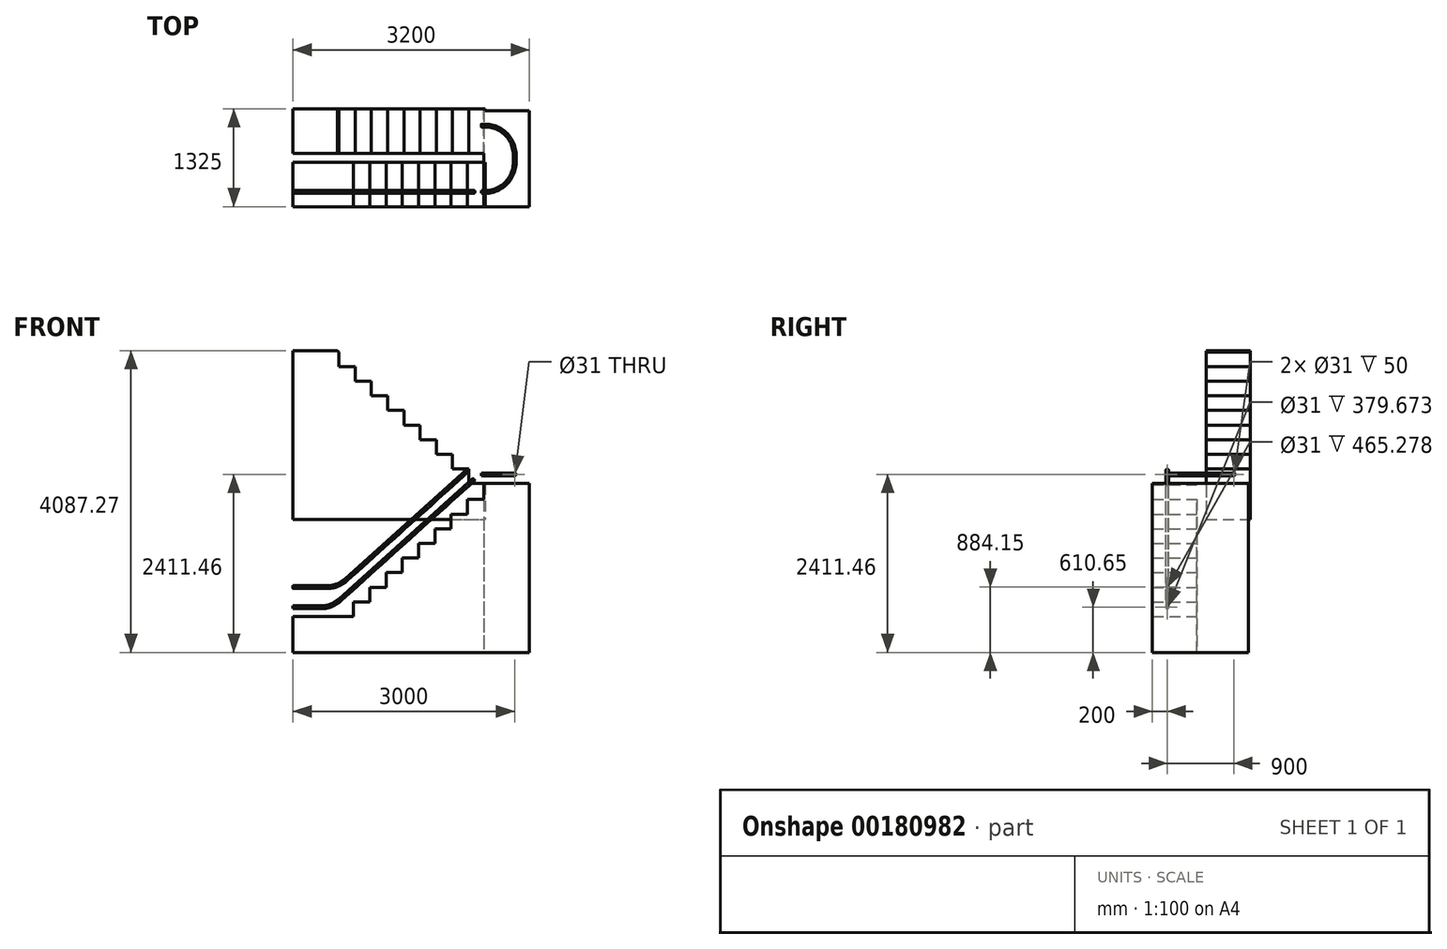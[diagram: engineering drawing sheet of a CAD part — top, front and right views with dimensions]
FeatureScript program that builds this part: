
annotation { "Feature Type Name" : "Feature", "Feature Type Description" : "" }
export const myFeature = defineFeature(function(context is Context, id is Id, definition is map)
    precondition{}
    {
        {
            var Q0;
            Q0=qCreatedBy(makeId("Front.planeOp"),FACE);
            var sketch = newSketch(context, id + "F0", { "sketchPlane" : qUnion([Q0])});
            skLineSegment(sketch, "E0", {"start": v(0, 0) * mm, "end": v(600, 0) * mm});
            skLineSegment(sketch, "E1", {"start": v(600, 0) * mm, "end": v(2600, 1800.8) * mm, "construction": true});
            skLineSegment(sketch, "E2", {"start": v(2600, 1800.8) * mm, "end": v(3200, 1800.8) * mm});
            skLineSegment(sketch, "E3", {"start": v(600, 0) * mm, "end": v(3446.75, 0) * mm, "construction": true});
            skLineSegment(sketch, "E4", {"start": v(716.2, 494.82) * mm, "end": v(803.08, 573.04) * mm});
            skPoint(sketch, "E5", {"position": v(759.64, 533.93) * mm});
            skPoint(sketch, "E6", {"position": v(655.57, 303.01) * mm});
            skCircle(sketch, "E7", {"center": v(655.57, 303.01) * mm, "radius": 25 * mm});
            skLineSegment(sketch, "E8", {"start": v(483.42, 114.37) * mm, "end": v(1236.08, 792.07) * mm});
            skLineSegment(sketch, "E9", {"start": v(627.76, 193.2) * mm, "end": v(1325.27, 821.24) * mm});
            skLineSegment(sketch, "E10", {"start": v(1036.91, 758.02) * mm, "end": v(1656.58, 1315.97) * mm});
            skLineSegment(sketch, "E11", {"start": v(940.91, 722.72) * mm, "end": v(2243.48, 1895.55) * mm});
            skLineSegment(sketch, "E12", {"start": v(415.28, 398.5) * mm, "end": v(465.28, 398.5) * mm});
            skArc(sketch, "E13", {"start": v(465.28, 398.5) * mm, "mid": v(599.67, 423.4) * mm, "end": v(716.2, 494.82) * mm});
            skLineSegment(sketch, "E14", {"start": v(465.28, 398.5) * mm, "end": v(465.28, 773.5) * mm, "construction": true});
            skLineSegment(sketch, "E15", {"start": v(465.28, 773.5) * mm, "end": v(716.2, 494.82) * mm, "construction": true});
            skLineSegment(sketch, "E16", {"start": v(0, 0) * mm, "end": v(0, 732.21) * mm, "construction": true});
            skLineSegment(sketch, "E17", {"start": v(415.28, 398.5) * mm, "end": v(0, 398.5) * mm});
            skLineSegment(sketch, "E18", {"start": v(630.6, 221.32) * mm, "end": v(1225.2, 756.7) * mm});
            skArc(sketch, "E19", {"start": v(379.67, 125) * mm, "mid": v(514.06, 149.9) * mm, "end": v(630.6, 221.32) * mm});
            skLineSegment(sketch, "E20", {"start": v(379.67, 125) * mm, "end": v(379.67, 500) * mm, "construction": true});
            skLineSegment(sketch, "E21", {"start": v(379.67, 500) * mm, "end": v(630.6, 221.32) * mm, "construction": true});
            skLineSegment(sketch, "E22", {"start": v(379.67, 125) * mm, "end": v(329.67, 125) * mm});
            skLineSegment(sketch, "E23", {"start": v(329.67, 125) * mm, "end": v(0, 125) * mm});
            skLineSegment(sketch, "E24", {"start": v(759.64, 533.93) * mm, "end": v(827.87, 458.15) * mm, "construction": true});
            skLineSegment(sketch, "E25", {"start": v(827.87, 458.15) * mm, "end": v(655.57, 303.01) * mm, "construction": true});
            skLineSegment(sketch, "E26", {"start": v(759.64, 533.93) * mm, "end": v(655.57, 303.01) * mm, "construction": true});
            skLineSegment(sketch, "E27", {"start": v(600, 0) * mm, "end": v(820, 0) * mm});
            skLineSegment(sketch, "E28", {"start": v(820, 0) * mm, "end": v(820, 198.09) * mm});
            skLineSegment(sketch, "E29", {"start": v(820, 198.09) * mm, "end": v(1040, 198.09) * mm});
            skLineSegment(sketch, "E30", {"start": v(1040, 198.09) * mm, "end": v(1040, 396.18) * mm});
            skLineSegment(sketch, "E31", {"start": v(1040, 396.18) * mm, "end": v(1260, 396.18) * mm});
            skLineSegment(sketch, "E32", {"start": v(1260, 396.18) * mm, "end": v(1260, 594.27) * mm});
            skLineSegment(sketch, "E33", {"start": v(3200, 1800.8) * mm, "end": v(3200, -485.65) * mm});
            skLineSegment(sketch, "E34", {"start": v(3200, -485.65) * mm, "end": v(0, -485.65) * mm});
            skLineSegment(sketch, "E35", {"start": v(0, -485.65) * mm, "end": v(0, 0) * mm});
            skPoint(sketch, "E36.start.orphan", {"position": v(1600, 900.4) * mm});
            skLineSegment(sketch, "E37", {"start": v(1260, 594.27) * mm, "end": v(1480, 594.27) * mm});
            skLineSegment(sketch, "E38", {"start": v(1480, 594.27) * mm, "end": v(1480, 792.36) * mm});
            skLineSegment(sketch, "E39", {"start": v(1480, 792.36) * mm, "end": v(1700, 792.36) * mm});
            skLineSegment(sketch, "E40", {"start": v(1700, 792.36) * mm, "end": v(1700, 990.44) * mm});
            skLineSegment(sketch, "E41", {"start": v(1700, 990.44) * mm, "end": v(1920, 990.44) * mm});
            skLineSegment(sketch, "E42", {"start": v(1920, 990.44) * mm, "end": v(1920, 1188.53) * mm});
            skLineSegment(sketch, "E43", {"start": v(1920, 1188.53) * mm, "end": v(2140, 1188.53) * mm});
            skLineSegment(sketch, "E44", {"start": v(2140, 1188.53) * mm, "end": v(2140, 1386.62) * mm});
            skLineSegment(sketch, "E45", {"start": v(2140, 1386.62) * mm, "end": v(2360, 1386.62) * mm});
            skLineSegment(sketch, "E46", {"start": v(2360, 1386.62) * mm, "end": v(2360, 1584.71) * mm});
            skLineSegment(sketch, "E47", {"start": v(2360, 1584.71) * mm, "end": v(2580, 1584.71) * mm});
            skLineSegment(sketch, "E48", {"start": v(2580, 1584.71) * mm, "end": v(2580, 1782.8) * mm});
            skLineSegment(sketch, "E49", {"start": v(2580, 1782.8) * mm, "end": v(2600, 1800.8) * mm});
            skLineSegment(sketch, "E50", {"start": v(803.08, 573.04) * mm, "end": v(2366.72, 1980.95) * mm});
            skLineSegment(sketch, "E51", {"start": v(1225.2, 756.7) * mm, "end": v(2449.59, 1859.15) * mm});
            skSolve(sketch);
        }
        {
            var Q0;
            Q0=qCreatedBy(makeId("Right.planeOp"),FACE);
            var sketch = newSketch(context, id + "F1", { "sketchPlane" : qUnion([Q0])});
            skLineSegment(sketch, "E52", {"start": v(0, 0) * mm, "end": v(0, 398.5) * mm, "construction": true});
            skPoint(sketch, "E53", {"position": v(0, 125) * mm});
            skCircle(sketch, "E54", {"center": v(0, 398.5) * mm, "radius": 19 * mm});
            skCircle(sketch, "E55", {"center": v(0, 125) * mm, "radius": 19 * mm});
            skCircle(sketch, "E56.0", {"center": v(0, 398.5) * mm, "radius": 15.5 * mm});
            skCircle(sketch, "E57.0", {"center": v(0, 125) * mm, "radius": 15.5 * mm});
            skSolve(sketch);
        }
        {
            var Q0;
            Q0=makeQuery(id+"F1.imprint","IMPRINT",FACE,{"disambiguationData":[TD([[makeQuery(id+"F1.imprint","IMPRINT",EDGE,{"derivedFrom":sQuery(id+"F1.wireOp",EDGE,"E54")}),1.0]])]});
            var Q1;
            Q1=sQuery(id+"F0.wireOp",EDGE,"E17");
            var Q2;
            Q2=sQuery(id+"F0.wireOp",EDGE,"E12");
            var Q3;
            Q3=sQuery(id+"F0.wireOp",EDGE,"E13");
            var Q4;
            Q4=sQuery(id+"F0.wireOp",EDGE,"E4");
            var Q5;
            Q5=sQuery(id+"F0.wireOp",EDGE,"E50");
            sweep(context, id + "F2", {"profiles" : qUnion([Q0]), "path" : qUnion([Q1, Q2, Q3, Q4, Q5])});
        }
        {
            var Q0;
            Q0=makeQuery(id+"F1.imprint","IMPRINT",FACE,{"disambiguationData":[TD([[makeQuery(id+"F1.imprint","IMPRINT",EDGE,{"derivedFrom":sQuery(id+"F1.wireOp",EDGE,"E55")}),1.0]])]});
            var Q1;
            Q1=sQuery(id+"F0.wireOp",EDGE,"E23");
            var Q2;
            Q2=sQuery(id+"F0.wireOp",EDGE,"E22");
            var Q3;
            Q3=sQuery(id+"F0.wireOp",EDGE,"E19");
            var Q4;
            Q4=sQuery(id+"F0.wireOp",EDGE,"E18");
            var Q5;
            Q5=sQuery(id+"F0.wireOp",EDGE,"E51");
            sweep(context, id + "F3", {"profiles" : qUnion([Q0]), "path" : qUnion([Q1, Q2, Q3, Q4, Q5])});
        }
        {
            var Q0;
            Q0=makeQuery(id+"F0.imprint","IMPRINT",FACE,{"disambiguationData":[TD([[makeQuery(id+"F0.imprint","IMPRINT",EDGE,{"derivedFrom":sQuery(id+"F0.wireOp",EDGE,"E0")}),-1.0]])]});
            extrude(context, id + "F4", {"entities" : qUnion([Q0]), "depth" : 200 * mm, "hasSecondDirection" : true, "secondDirectionOppositeDirection" : true, "secondDirectionDepth" : 400 * mm});
        }
        {
            var Q0;
            Q0=makeQuery(id+"F4.opExtrude","CAP_FACE",FACE,{"disambiguationData":[OSD([sQuery(id+"F0.wireOp",EDGE,"E0"),sQuery(id+"F0.wireOp",EDGE,"E2"),sQuery(id+"F0.wireOp",EDGE,"E27"),sQuery(id+"F0.wireOp",EDGE,"E28"),sQuery(id+"F0.wireOp",EDGE,"E29"),sQuery(id+"F0.wireOp",EDGE,"E30"),sQuery(id+"F0.wireOp",EDGE,"E31"),sQuery(id+"F0.wireOp",EDGE,"E32"),sQuery(id+"F0.wireOp",EDGE,"E33"),sQuery(id+"F0.wireOp",EDGE,"E34"),sQuery(id+"F0.wireOp",EDGE,"E35"),sQuery(id+"F0.wireOp",EDGE,"E37"),sQuery(id+"F0.wireOp",EDGE,"E38"),sQuery(id+"F0.wireOp",EDGE,"E39"),sQuery(id+"F0.wireOp",EDGE,"E40"),sQuery(id+"F0.wireOp",EDGE,"E41"),sQuery(id+"F0.wireOp",EDGE,"E42"),sQuery(id+"F0.wireOp",EDGE,"E43"),sQuery(id+"F0.wireOp",EDGE,"E44"),sQuery(id+"F0.wireOp",EDGE,"E45"),sQuery(id+"F0.wireOp",EDGE,"E46"),sQuery(id+"F0.wireOp",EDGE,"E47"),sQuery(id+"F0.wireOp",EDGE,"E48"),sQuery(id+"F0.wireOp",EDGE,"E49")])],"isStart":true});
            var sketch = newSketch(context, id + "F5", { "sketchPlane" : qUnion([Q0])});
            skLineSegment(sketch, "E58.bottom", {"start": v(-3200, 1800.8) * mm, "end": v(-2580, 1800.8) * mm});
            skLineSegment(sketch, "E58.top", {"start": v(-3200, -485.65) * mm, "end": v(-2580, -485.65) * mm});
            skLineSegment(sketch, "E58.left", {"start": v(-3200, 1800.8) * mm, "end": v(-3200, -485.65) * mm});
            skLineSegment(sketch, "E58.right", {"start": v(-2580, 1800.8) * mm, "end": v(-2580, -485.65) * mm});
            skSolve(sketch);
        }
        {
            var Q0;
            Q0 = qSketchRegion(id + "F5", true);
            extrude(context, id + "F6", {"entities" : qUnion([Q0]), "operationType" : NewBodyOperationType.ADD, "depth" : 700 * mm});
        }
        {
            var Q0;
            Q0=makeQuery(id+"F6.opExtrude","CAP_FACE",FACE,{"disambiguationData":[OSD([sQuery(id+"F5.wireOp",EDGE,"E58.bottom"),sQuery(id+"F5.wireOp",EDGE,"E58.top"),sQuery(id+"F5.wireOp",EDGE,"E58.left"),sQuery(id+"F5.wireOp",EDGE,"E58.right")])],"isStart":false});
            cPlane(context, id + "F7", {"entities" : qUnion([Q0]), "cplaneType" : CPlaneType.OFFSET, "offset" : 25 * mm, "width" : 150 * mm, "height" : 150 * mm});
        }
        {
            var Q0;
            Q0=qCreatedBy(id+"F7.planeOp",FACE);
            var sketch = newSketch(context, id + "F8", { "sketchPlane" : qUnion([Q0])});
            skLineSegment(sketch, "E59", {"start": v(-3200, 1800.8) * mm, "end": v(-2600, 1800.8) * mm});
            skLineSegment(sketch, "E60", {"start": v(-2600, 1800.8) * mm, "end": v(-600, 3601.62) * mm, "construction": true});
            skLineSegment(sketch, "E61", {"start": v(-600, 3601.62) * mm, "end": v(0, 3601.62) * mm});
            skLineSegment(sketch, "E62", {"start": v(-2600, 1800.8) * mm, "end": v(246.75, 1800.8) * mm, "construction": true});
            skLineSegment(sketch, "E63", {"start": v(-2600, 1800.8) * mm, "end": v(-2380, 1800.8) * mm});
            skLineSegment(sketch, "E64", {"start": v(-2380, 1800.8) * mm, "end": v(-2380, 1998.9) * mm});
            skLineSegment(sketch, "E65", {"start": v(-2380, 1998.9) * mm, "end": v(-2160, 1998.9) * mm});
            skLineSegment(sketch, "E66", {"start": v(-2160, 1998.9) * mm, "end": v(-2160, 2196.99) * mm});
            skLineSegment(sketch, "E67", {"start": v(-2160, 2196.99) * mm, "end": v(-1940, 2196.99) * mm});
            skLineSegment(sketch, "E68", {"start": v(-1940, 2196.99) * mm, "end": v(-1940, 2395.07) * mm});
            skLineSegment(sketch, "E69", {"start": v(0, 3601.62) * mm, "end": v(0, 1315.16) * mm});
            skLineSegment(sketch, "E70", {"start": v(0, 1315.16) * mm, "end": v(-3200, 1315.16) * mm});
            skLineSegment(sketch, "E71", {"start": v(-3200, 1315.16) * mm, "end": v(-3200, 1800.8) * mm});
            skPoint(sketch, "E72.start.orphan", {"position": v(-1600, 2701.21) * mm});
            skLineSegment(sketch, "E73", {"start": v(-1940, 2395.07) * mm, "end": v(-1720, 2395.07) * mm});
            skLineSegment(sketch, "E74", {"start": v(-1720, 2395.07) * mm, "end": v(-1720, 2593.16) * mm});
            skLineSegment(sketch, "E75", {"start": v(-1720, 2593.16) * mm, "end": v(-1500, 2593.16) * mm});
            skLineSegment(sketch, "E76", {"start": v(-1500, 2593.16) * mm, "end": v(-1500, 2791.25) * mm});
            skLineSegment(sketch, "E77", {"start": v(-1500, 2791.25) * mm, "end": v(-1280, 2791.25) * mm});
            skLineSegment(sketch, "E78", {"start": v(-1280, 2791.25) * mm, "end": v(-1280, 2989.34) * mm});
            skLineSegment(sketch, "E79", {"start": v(-1280, 2989.34) * mm, "end": v(-1060, 2989.34) * mm});
            skLineSegment(sketch, "E80", {"start": v(-1060, 2989.34) * mm, "end": v(-1060, 3187.43) * mm});
            skLineSegment(sketch, "E81", {"start": v(-1060, 3187.43) * mm, "end": v(-840, 3187.43) * mm});
            skLineSegment(sketch, "E82", {"start": v(-840, 3187.43) * mm, "end": v(-840, 3385.52) * mm});
            skLineSegment(sketch, "E83", {"start": v(-840, 3385.52) * mm, "end": v(-620, 3385.52) * mm});
            skLineSegment(sketch, "E84", {"start": v(-620, 3385.52) * mm, "end": v(-620, 3583.6) * mm});
            skLineSegment(sketch, "E85", {"start": v(-620, 3583.6) * mm, "end": v(-600, 3601.62) * mm});
            skLineSegment(sketch, "E86", {"start": v(-2600, 1800.8) * mm, "end": v(-2600, 1315.16) * mm});
            skSolve(sketch);
        }
        {
            var Q0;
            Q0=makeQuery(id+"F8.imprint","IMPRINT",FACE,{"disambiguationData":[TD([[makeQuery(id+"F8.imprint","IMPRINT",EDGE,{"derivedFrom":sQuery(id+"F8.wireOp",EDGE,"E61")}),-1.0]])]});
            extrude(context, id + "F9", {"entities" : qUnion([Q0]), "operationType" : NewBodyOperationType.ADD, "oppositeDirection" : true, "depth" : 600 * mm});
        }
        {
            var Q0;
            Q0=makeQuery(id+"F9.boolean.opBoolean","MERGE",FACE,{"derivedFrom":[makeQuery(id+"F6.boolean.opBoolean","MERGE",FACE,{"derivedFrom":[makeQuery(id+"F4.opExtrude","SWEPT_FACE",FACE,{"disambiguationData":[OSD([sQuery(id+"F0.wireOp",EDGE,"E2")])]}),makeQuery(id+"F6.opExtrude","SWEPT_FACE",FACE,{"disambiguationData":[OSD([sQuery(id+"F5.wireOp",EDGE,"E58.bottom")])]})]}),makeQuery(id+"F9.opExtrude","SWEPT_FACE",FACE,{"disambiguationData":[OSD([sQuery(id+"F8.wireOp",EDGE,"E63")])]})]});
            cPlane(context, id + "F10", {"entities" : qUnion([Q0]), "cplaneType" : CPlaneType.OFFSET, "offset" : 125 * mm, "width" : 150 * mm, "height" : 150 * mm});
        }
        {
            var Q0;
            Q0=qCreatedBy(id+"F10.planeOp",FACE);
            var sketch = newSketch(context, id + "F11", { "sketchPlane" : qUnion([Q0])});
            skLineSegment(sketch, "E87.bottom", {"start": v(2550, 0) * mm, "end": v(2600, 0) * mm});
            skLineSegment(sketch, "E87.top", {"start": v(2550, 900) * mm, "end": v(2600, 900) * mm});
            skLineSegment(sketch, "E87.right", {"start": v(3000, 400) * mm, "end": v(3000, 500) * mm});
            skPoint(sketch, "E88.visualSharp", {"position": v(3000, 900) * mm});
            skArc(sketch, "E88.filletArc", {"start": v(3000, 500) * mm, "mid": v(2882.84, 782.84) * mm, "end": v(2600, 900) * mm});
            skPoint(sketch, "E89.visualSharp", {"position": v(3000, 0) * mm});
            skArc(sketch, "E89.filletArc", {"start": v(2600, 0) * mm, "mid": v(2882.84, 117.16) * mm, "end": v(3000, 400) * mm});
            skPoint(sketch, "E90", {"position": v(3000, 450) * mm});
            skSolve(sketch);
        }
        {
            var Q0;
            Q0=makeQuery(id+"F6.boolean.opBoolean","MERGE",FACE,{"derivedFrom":[makeQuery(id+"F4.opExtrude","SWEPT_FACE",FACE,{"disambiguationData":[OSD([sQuery(id+"F0.wireOp",EDGE,"E48")])]}),makeQuery(id+"F6.opExtrude","SWEPT_FACE",FACE,{"disambiguationData":[OSD([sQuery(id+"F5.wireOp",EDGE,"E58.right")])]})]});
            var Q1;
            Q1=sQuery(id+"F11.wireOp",VERTEX,"E87.bottom.start");
            cPlane(context, id + "F12", {"entities" : qUnion([Q0, Q1]), "cplaneType" : CPlaneType.PLANE_POINT, "offset" : 25 * mm, "width" : 150 * mm, "height" : 150 * mm});
        }
        {
            var Q0;
            Q0=qCreatedBy(id+"F12.planeOp",FACE);
            var sketch = newSketch(context, id + "F13", { "sketchPlane" : qUnion([Q0])});
            skCircle(sketch, "E91", {"center": v(0, 1925.8) * mm, "radius": 19 * mm});
            skCircle(sketch, "E92.0", {"center": v(0, 1925.8) * mm, "radius": 15.5 * mm});
            skSolve(sketch);
        }
        {
            var Q0;
            Q0=makeQuery(id+"F13.imprint","IMPRINT",FACE,{"disambiguationData":[TD([[makeQuery(id+"F13.imprint","IMPRINT",EDGE,{"derivedFrom":sQuery(id+"F13.wireOp",EDGE,"E91")}),1.0]])]});
            var Q1;
            Q1=sQuery(id+"F11.wireOp",EDGE,"E87.bottom");
            var Q2;
            Q2=sQuery(id+"F11.wireOp",EDGE,"E89.filletArc");
            var Q3;
            Q3=sQuery(id+"F11.wireOp",EDGE,"E87.right");
            var Q4;
            Q4=sQuery(id+"F11.wireOp",EDGE,"E88.filletArc");
            var Q5;
            Q5=sQuery(id+"F11.wireOp",EDGE,"E87.top");
            sweep(context, id + "F14", {"profiles" : qUnion([Q0]), "path" : qUnion([Q1, Q2, Q3, Q4, Q5])});
        }
    });
